# Revit family: BE_77155_de_DE
name_source: partatom
category: Leuchten
revit_build: Autodesk Revit 2015 (Build: 20160512_0715(x64)
units: mm (PartAtom-declared; Revit-internal decimal feet)

## types (4) — shared parameters
AC/DC = AC/DC
Aktualisierung = 2017-01-26T04:13:31
Anschlussleitung = 0.5 m X05BQ-F 5 G 1²
BEGA_Dummy = Nein
BEGA_IES = Ja
BEGA_Intern = Ja
BEGA_Intern_Konstruktion = Ja
BEGA_Intern_an = Ja
BEGA_Intern_aus = Ja
Befestigungsabstand = 880 mm
Befestigungsbohrung = Ø 7 mm
Beschreibung = Fassadenscheinwerfer
Beschreibung_Sonderanfertigung = Hier können Sie Informationen zur Sonderanfertigung eintragen.
CE_Konformität = ja
Energieeffizienzklasse = LED A++ - A
Farbfilter = 16777215
Farbtemperaturverschiebung bei Dämpfen der Lampe = <Keine Auswahl>
Farbwiedergabeindex = Ra > 80
Frequenz = 0/50-60 Hz
Gewicht = 5.5 kg
Hersteller = BEGA
Lampe = LED 33.6 W
Lastklassifizierung = Beleuchtung
Lebensdauerkriterien = L70 = 50.000 h
Logo = BEGA_Logo.png
M_W = Nein
Material_02 = BEGA_Oberfläche_Silber_matt
Material_03 = BEGA_Oberfläche_Weiss_matt
Material_04 = BEGA_Kunststoff_Grafit_matt
Material_06 = BEGA_Oberfläche_Edelstahl_gebürstet
Material_09 = BEGA_Glas_klar
Material_10 = BEGA_Glas_matt
Material_11 = BEGA_Glas_opal
Material_15 = BEGA_Leuchtmedium_matt
Material_17 = BEGA_Reflektor
Material_18 = BEGA_Gummi_schwarz
Neigungswinkel = 0.00°
Produktdatenblatt = http://www.bega.de
Scheinlast = 0 VA
Schutzart = IP 65
Schutzklasse = I
Sonderanfertigung = Nein
Spannung = 240 V
Typenbild = 77155.png
URL = http://www.bega.de
zero-valued in all types: Vorgabe-Ansicht

## per-type parameters (varying)
| type | Bestellnummer | Datei für fotometrisches Netz | Farbtemperatur | LED_Modulbezeichnung | Lampenlichtstrom | Leuchtenlichtstrom | M_A | M_G | Modell |
| BEGA_77155_Grafit_K4 | 77155 | BE_77155.IES | 4000 K | 2x LED-0612/840 | 4950 lm | 2565 lm | Nein | Ja | 77155 |
| BEGA_77155_Silber_K4 | 77155A | BE_77155.IES | 4000 K | 2x LED-0612/840 | 4950 lm | 2565 lm | Ja | Nein | 77155A |
| BEGA_77155_Silber_K3 | 77155AK3 | BE_77155K3.IES | 3000 K | 2x LED-0612/830 | 4530 lm | 2347 lm | Ja | Nein | 77155AK3 |
| BEGA_77155_Grafit_K3 | 77155K3 | BE_77155K3.IES | 3000 K | 2x LED-0612/830 | 4530 lm | 2347 lm | Nein | Ja | 77155K3 |
